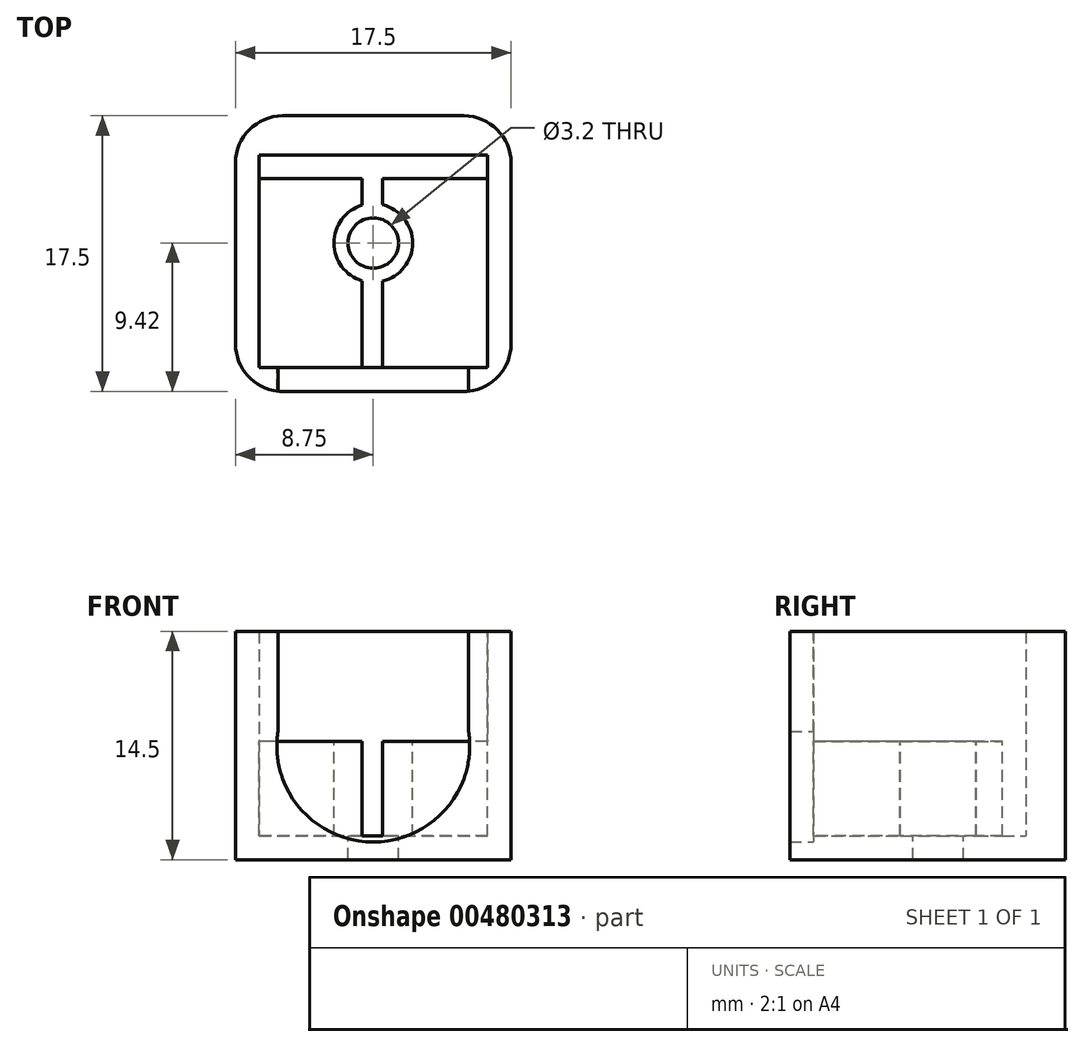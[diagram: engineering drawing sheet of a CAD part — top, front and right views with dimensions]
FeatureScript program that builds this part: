
annotation { "Feature Type Name" : "Feature", "Feature Type Description" : "" }
export const myFeature = defineFeature(function(context is Context, id is Id, definition is map)
    precondition{}
    {
        {
            var Q0;
            Q0=qCreatedBy(makeId("Front.planeOp"),FACE);
            var sketch = newSketch(context, id + "F0", { "sketchPlane" : qUnion([Q0])});
            skLineSegment(sketch, "E0.bottom", {"start": v(-7.25, 7.25) * mm, "end": v(7.25, 7.25) * mm});
            skLineSegment(sketch, "E0.top", {"start": v(-7.25, -7.25) * mm, "end": v(7.25, -7.25) * mm});
            skLineSegment(sketch, "E0.left", {"start": v(-7.25, 7.25) * mm, "end": v(-7.25, -7.25) * mm});
            skLineSegment(sketch, "E0.right", {"start": v(7.25, 7.25) * mm, "end": v(7.25, -7.25) * mm});
            skPoint(sketch, "E0.middle", {"position": v(0, 0) * mm});
            skEllipse(sketch, "E1", {"center": v(0, 0) * mm, "majorRadius": 6.12 * mm, "minorRadius": 6.13 * mm, "majorAxis": v(1, 0)});
            skLineSegment(sketch, "E2", {"start": v(-6.06, 0.91) * mm, "end": v(-6.06, 7.25) * mm});
            skLineSegment(sketch, "E3", {"start": v(6.06, 0.91) * mm, "end": v(6.06, 7.25) * mm});
            skSolve(sketch);
        }
        {
            var Q0;
            Q0=makeQuery(id+"F0.imprint","IMPRINT",FACE,{"disambiguationData":[TD([[makeQuery(id+"F0.imprint","IMPRINT",EDGE,{"derivedFrom":sQuery(id+"F0.wireOp",EDGE,"E0.bottom")}),-1.0]])]});
            extrude(context, id + "F1", {"entities" : qUnion([Q0]), "depth" : 1.5 * mm, "offsetDistance" : 25 * mm});
        }
        {
            var Q0;
            Q0=makeQuery(id+"F1.opExtrude","SWEPT_FACE",FACE,{"disambiguationData":[OSD([sQuery(id+"F0.wireOp",EDGE,"E0.right")])]});
            var sketch = newSketch(context, id + "F2", { "sketchPlane" : qUnion([Q0])});
            skLineSegment(sketch, "E4.0", {"start": v(-1.5, 7.25) * mm, "end": v(-1.5, -7.25) * mm});
            skLineSegment(sketch, "E5", {"start": v(-1.5, 7.25) * mm, "end": v(13.5, 7.25) * mm});
            skLineSegment(sketch, "E6", {"start": v(-1.5, -7.25) * mm, "end": v(13.5, -7.25) * mm});
            skPoint(sketch, "E6.endSnap0", {"position": v(-0.75, -7.25) * mm});
            skLineSegment(sketch, "E7", {"start": v(13.5, -7.25) * mm, "end": v(13.5, 7.25) * mm});
            skSolve(sketch);
        }
        {
            var Q0;
            {var subQ2=sQuery(id+"F2.wireOp",EDGE,"E7");Q0=makeQuery(id+"F2.imprint","IMPRINT",FACE,{"disambiguationData":[TD([[makeQuery(id+"F2.imprint","IMPRINT",EDGE,{"derivedFrom":subQ2}),1.0]])]});}
            var Q1;
            {var subQ0=sQuery(id+"F2.wireOp",EDGE,"E4.0");Q1=makeQuery(id+"F2.imprint","IMPRINT",FACE,{"disambiguationData":[TD([[makeQuery(id+"F2.imprint","IMPRINT",EDGE,{"derivedFrom":subQ0}),1.0]])]});}
            extrude(context, id + "F3", {"entities" : qUnion([Q0, Q1]), "operationType" : NewBodyOperationType.ADD, "depth" : 1.5 * mm, "offsetDistance" : 25 * mm});
        }
        {
            var Q0;
            Q0=makeQuery(id+"F1.opExtrude","SWEPT_FACE",FACE,{"disambiguationData":[OSD([sQuery(id+"F0.wireOp",EDGE,"E0.left")])]});
            var sketch = newSketch(context, id + "F4", { "sketchPlane" : qUnion([Q0])});
            skLineSegment(sketch, "E8.0", {"start": v(1.5, 7.25) * mm, "end": v(1.5, -7.25) * mm});
            skLineSegment(sketch, "E9", {"start": v(1.5, 7.25) * mm, "end": v(-13.5, 7.25) * mm});
            skLineSegment(sketch, "E10", {"start": v(-13.5, 7.25) * mm, "end": v(-13.5, -7.25) * mm});
            skLineSegment(sketch, "E11", {"start": v(-13.5, -7.25) * mm, "end": v(1.5, -7.25) * mm});
            skSolve(sketch);
        }
        {
            var Q0;
            {var subQ0=sQuery(id+"F4.wireOp",EDGE,"E8.0");Q0=makeQuery(id+"F4.imprint","IMPRINT",FACE,{"disambiguationData":[TD([[makeQuery(id+"F4.imprint","IMPRINT",EDGE,{"derivedFrom":subQ0}),-1.0]])]});}
            var Q1;
            {var subQ2=sQuery(id+"F4.wireOp",EDGE,"E10");Q1=makeQuery(id+"F4.imprint","IMPRINT",FACE,{"disambiguationData":[TD([[makeQuery(id+"F4.imprint","IMPRINT",EDGE,{"derivedFrom":subQ2}),1.0]])]});}
            extrude(context, id + "F5", {"entities" : qUnion([Q0, Q1]), "operationType" : NewBodyOperationType.ADD, "depth" : 1.5 * mm, "offsetDistance" : 25 * mm});
        }
        {
            var Q0;
            Q0=makeQuery(id+"F5.opExtrude","SWEPT_FACE",FACE,{"disambiguationData":[OSD([sQuery(id+"F4.wireOp",EDGE,"E10")])]});
            var sketch = newSketch(context, id + "F6", { "sketchPlane" : qUnion([Q0])});
            skLineSegment(sketch, "E12.0", {"start": v(-8.75, -7.25) * mm, "end": v(-8.75, 7.25) * mm});
            skLineSegment(sketch, "E13.0", {"start": v(8.75, 7.25) * mm, "end": v(8.75, -7.25) * mm});
            skLineSegment(sketch, "E14", {"start": v(-8.75, 7.25) * mm, "end": v(8.75, 7.25) * mm});
            skLineSegment(sketch, "E15", {"start": v(8.75, -7.25) * mm, "end": v(-8.75, -7.25) * mm});
            skSolve(sketch);
        }
        {
            var Q0;
            {var subQ0=sQuery(id+"F6.wireOp",EDGE,"E12.0");Q0=makeQuery(id+"F6.imprint","IMPRINT",FACE,{"disambiguationData":[TD([[makeQuery(id+"F6.imprint","IMPRINT",EDGE,{"derivedFrom":subQ0}),-1.0]])]});}
            var Q1;
            {var subQ0=sQuery(id+"F6.wireOp",EDGE,"E13.0");Q1=makeQuery(id+"F6.imprint","IMPRINT",FACE,{"disambiguationData":[TD([[makeQuery(id+"F6.imprint","IMPRINT",EDGE,{"derivedFrom":subQ0}),-1.0]])]});}
            extrude(context, id + "F7", {"entities" : qUnion([Q0, Q1]), "operationType" : NewBodyOperationType.ADD, "depth" : 2.5 * mm, "offsetDistance" : 25 * mm});
        }
        {
            var Q0;
            Q0=makeQuery(id+"F7.boolean.opBoolean","MERGE",FACE,{"derivedFrom":[makeQuery(id+"F5.boolean.opBoolean","MERGE",FACE,{"derivedFrom":[makeQuery(id+"F3.boolean.opBoolean","MERGE",FACE,{"derivedFrom":[makeQuery(id+"F1.opExtrude","SWEPT_FACE",FACE,{"disambiguationData":[OSD([sQuery(id+"F0.wireOp",EDGE,"E0.top")])]}),makeQuery(id+"F3.opExtrude","SWEPT_FACE",FACE,{"disambiguationData":[OSD([sQuery(id+"F2.wireOp",EDGE,"E6")])]})]}),makeQuery(id+"F5.opExtrude","SWEPT_FACE",FACE,{"disambiguationData":[OSD([sQuery(id+"F4.wireOp",EDGE,"E11")])]})]}),makeQuery(id+"F7.opExtrude","SWEPT_FACE",FACE,{"disambiguationData":[OSD([sQuery(id+"F6.wireOp",EDGE,"E15")])]})]});
            var sketch = newSketch(context, id + "F8", { "sketchPlane" : qUnion([Q0])});
            skPoint(sketch, "E16.0", {"position": v(0, -13.5) * mm});
            skLineSegment(sketch, "E17.0", {"start": v(-7.25, -13.5) * mm, "end": v(7.25, -13.5) * mm});
            skLineSegment(sketch, "E18.0", {"start": v(7.25, 0) * mm, "end": v(7.25, -13.5) * mm});
            skLineSegment(sketch, "E19.0", {"start": v(-7.25, 0) * mm, "end": v(7.25, 0) * mm});
            skLineSegment(sketch, "E20.0", {"start": v(-7.25, 0) * mm, "end": v(-7.25, -13.5) * mm});
            skSolve(sketch);
        }
        {
            var Q0;
            Q0=makeQuery(id+"F8.imprint","IMPRINT",FACE,{"disambiguationData":[TD([[makeQuery(id+"F8.imprint","IMPRINT",EDGE,{"derivedFrom":sQuery(id+"F8.wireOp",EDGE,"E17.0")}),1.0]])]});
            extrude(context, id + "F9", {"entities" : qUnion([Q0]), "operationType" : NewBodyOperationType.ADD, "oppositeDirection" : true, "depth" : 1.5 * mm, "offsetDistance" : 25 * mm});
        }
        {
            var Q0;
            Q0=makeQuery(id+"F5.opExtrude","CAP_FACE",FACE,{"disambiguationData":[OSD([sQuery(id+"F4.wireOp",EDGE,"E8.0"),sQuery(id+"F4.wireOp",EDGE,"E9"),sQuery(id+"F4.wireOp",EDGE,"E10"),sQuery(id+"F4.wireOp",EDGE,"E11")])],"isStart":true});
            var sketch = newSketch(context, id + "F10", { "sketchPlane" : qUnion([Q0])});
            skLineSegment(sketch, "E21.0", {"start": v(13.5, 7.25) * mm, "end": v(13.5, -5.75) * mm});
            skLineSegment(sketch, "E22.0", {"start": v(0, -5.75) * mm, "end": v(13.5, -5.75) * mm});
            skLineSegment(sketch, "E23.0", {"start": v(0, 7.25) * mm, "end": v(13.5, 7.25) * mm});
            skLineSegment(sketch, "E24.0", {"start": v(0, 6.25) * mm, "end": v(0, -5.75) * mm});
            skLineSegment(sketch, "E25", {"start": v(12, -5.75) * mm, "end": v(12, 0.25) * mm});
            skLineSegment(sketch, "E26", {"start": v(12, 0.25) * mm, "end": v(0, 0.25) * mm});
            skLineSegment(sketch, "E27", {"start": v(0, 0.25) * mm, "end": v(0, -5.75) * mm});
            skSolve(sketch);
        }
        {
            var Q0;
            {var subQ0=sQuery(id+"F10.wireOp",EDGE,"E25");Q0=makeQuery(id+"F10.imprint","IMPRINT",FACE,{"disambiguationData":[TD([[makeQuery(id+"F10.imprint","IMPRINT",EDGE,{"derivedFrom":subQ0}),1.0]])]});}
            var Q1;
            Q1=makeQuery(id+"F3.opExtrude","CAP_FACE",FACE,{"disambiguationData":[OSD([sQuery(id+"F2.wireOp",EDGE,"E4.0"),sQuery(id+"F2.wireOp",EDGE,"E5"),sQuery(id+"F2.wireOp",EDGE,"E6"),sQuery(id+"F2.wireOp",EDGE,"E7")])],"isStart":true});
            extrude(context, id + "F11", {"entities" : qUnion([Q0]), "operationType" : NewBodyOperationType.ADD, "endBound" : BoundingType.UP_TO_SURFACE, "endBoundEntityFace" : qUnion([Q1]), "depth" : 25 * mm, "offsetDistance" : 25 * mm});
        }
        {
            var Q0;
            Q0=makeQuery(id+"F11.opExtrude","SWEPT_FACE",FACE,{"disambiguationData":[OSD([sQuery(id+"F10.wireOp",EDGE,"E26")])]});
            var sketch = newSketch(context, id + "F12", { "sketchPlane" : qUnion([Q0])});
            skLineSegment(sketch, "E28.0", {"start": v(7.25, 12) * mm, "end": v(-7.25, 12) * mm});
            skLineSegment(sketch, "E29.0", {"start": v(51.12, 0) * mm, "end": v(-51.12, 0) * mm});
            skLineSegment(sketch, "E30", {"start": v(-0.7, 12) * mm, "end": v(-0.7, 0) * mm});
            skLineSegment(sketch, "E31", {"start": v(-0.7, 0) * mm, "end": v(0.6, 0) * mm});
            skLineSegment(sketch, "E32", {"start": v(0.6, 0) * mm, "end": v(0.6, 12) * mm});
            skLineSegment(sketch, "E33", {"start": v(0.6, 12) * mm, "end": v(-0.7, 12) * mm});
            skSolve(sketch);
        }
        {
            var Q0;
            Q0=makeQuery(id+"F12.imprint","IMPRINT",FACE,{"disambiguationData":[TD([[makeQuery(id+"F12.imprint","IMPRINT",EDGE,{"derivedFrom":sQuery(id+"F12.wireOp",EDGE,"E30")}),1.0]])]});
            var Q1;
            Q1=makeQuery(id+"F11.boolean.opBoolean","SPLIT",FACE,{"disambiguationData":[TD([makeQuery(id+"F11.opExtrude","SWEPT_FACE",FACE,{"disambiguationData":[OSD([sQuery(id+"F10.wireOp",EDGE,"E25")])]})])],"derivedFrom":makeQuery(id+"F9.opExtrude","CAP_FACE",FACE,{"disambiguationData":[OSD([sQuery(id+"F8.wireOp",EDGE,"E17.0"),sQuery(id+"F8.wireOp",EDGE,"E18.0"),sQuery(id+"F8.wireOp",EDGE,"E19.0"),sQuery(id+"F8.wireOp",EDGE,"E20.0")])],"isStart":false})});
            extrude(context, id + "F13", {"entities" : qUnion([Q0]), "operationType" : NewBodyOperationType.REMOVE, "endBound" : BoundingType.UP_TO_SURFACE, "oppositeDirection" : true, "endBoundEntityFace" : qUnion([Q1]), "depth" : 25.4 * mm});
        }
        {
            var Q0;
            {var subQ0=sQuery(id+"F0.wireOp",EDGE,"E0.bottom");Q0=makeQuery(id+"F7.boolean.opBoolean","MERGE",FACE,{"derivedFrom":[makeQuery(id+"F3.boolean.opBoolean","MERGE",FACE,{"derivedFrom":[makeQuery(id+"F1.opExtrude","SWEPT_FACE",FACE,{"disambiguationData":[OSD([subQ0]),TDD([makeQuery(id+"F0.imprint","IMPRINT",EDGE,{"disambiguationData":[TD([[makeQuery(id+"F0.imprint","INTERSECT",VERTEX,{"derivedFrom":[subQ0,sQuery(id+"F0.wireOp",EDGE,"E0.right")]}),1.0]])],"derivedFrom":subQ0})])]}),makeQuery(id+"F3.opExtrude","SWEPT_FACE",FACE,{"disambiguationData":[OSD([sQuery(id+"F2.wireOp",EDGE,"E5")])]})]}),makeQuery(id+"F5.boolean.opBoolean","MERGE",FACE,{"derivedFrom":[makeQuery(id+"F1.opExtrude","SWEPT_FACE",FACE,{"disambiguationData":[OSD([subQ0]),TDD([makeQuery(id+"F0.imprint","IMPRINT",EDGE,{"disambiguationData":[TD([[makeQuery(id+"F0.imprint","INTERSECT",VERTEX,{"derivedFrom":[subQ0,sQuery(id+"F0.wireOp",EDGE,"E0.left")]}),-1.0]])],"derivedFrom":subQ0})])]}),makeQuery(id+"F5.opExtrude","SWEPT_FACE",FACE,{"disambiguationData":[OSD([sQuery(id+"F4.wireOp",EDGE,"E9")])]})]}),makeQuery(id+"F7.opExtrude","SWEPT_FACE",FACE,{"disambiguationData":[OSD([sQuery(id+"F6.wireOp",EDGE,"E14")])]})]});}
            var sketch = newSketch(context, id + "F14", { "sketchPlane" : qUnion([Q0])});
            skCircle(sketch, "E34", {"center": v(0, 7.92) * mm, "radius": 2.5 * mm});
            skCircle(sketch, "E35", {"center": v(0, 7.92) * mm, "radius": 1.6 * mm});
            skSolve(sketch);
        }
        {
            var Q0;
            Q0=makeQuery(id+"F14.imprint","IMPRINT",FACE,{"disambiguationData":[TD([[makeQuery(id+"F14.imprint","IMPRINT",EDGE,{"derivedFrom":sQuery(id+"F14.wireOp",EDGE,"E34")}),1.0]])]});
            var Q1;
            {var subQ2=makeQuery(id+"F9.opExtrude","CAP_FACE",FACE,{"disambiguationData":[OSD([sQuery(id+"F8.wireOp",EDGE,"E17.0"),sQuery(id+"F8.wireOp",EDGE,"E18.0"),sQuery(id+"F8.wireOp",EDGE,"E19.0"),sQuery(id+"F8.wireOp",EDGE,"E20.0")])],"isStart":false});Q1=makeQuery(id+"F13.boolean.opBoolean","MERGE",FACE,{"derivedFrom":[makeQuery(id+"F11.boolean.opBoolean","SPLIT",FACE,{"disambiguationData":[TD([makeQuery(id+"F11.opExtrude","SWEPT_FACE",FACE,{"disambiguationData":[OSD([sQuery(id+"F10.wireOp",EDGE,"E25")])]})])],"derivedFrom":subQ2}),makeQuery(id+"F11.boolean.opBoolean","SPLIT",FACE,{"disambiguationData":[TD([makeQuery(id+"F11.opExtrude","SWEPT_FACE",FACE,{"disambiguationData":[OSD([sQuery(id+"F10.wireOp",EDGE,"E27")])]})])],"derivedFrom":subQ2}),makeQuery(id+"F13.opExtrude","CAP_FACE",FACE,{"disambiguationData":[OSD([sQuery(id+"F12.wireOp",EDGE,"E30"),sQuery(id+"F12.wireOp",EDGE,"E31"),sQuery(id+"F12.wireOp",EDGE,"E32"),sQuery(id+"F12.wireOp",EDGE,"E33")])],"isStart":false})]});}
            extrude(context, id + "F15", {"entities" : qUnion([Q0]), "operationType" : NewBodyOperationType.REMOVE, "endBound" : BoundingType.UP_TO_SURFACE, "oppositeDirection" : true, "endBoundEntityFace" : qUnion([Q1]), "depth" : 25 * mm, "offsetDistance" : 25 * mm});
        }
        {
            var Q0;
            Q0=makeQuery(id+"F14.imprint","IMPRINT",FACE,{"disambiguationData":[TD([[makeQuery(id+"F14.imprint","IMPRINT",EDGE,{"derivedFrom":sQuery(id+"F14.wireOp",EDGE,"E35")}),1.0]])]});
            extrude(context, id + "F16", {"entities" : qUnion([Q0]), "operationType" : NewBodyOperationType.REMOVE, "endBound" : BoundingType.THROUGH_ALL, "oppositeDirection" : true, "depth" : 25 * mm, "offsetDistance" : 25 * mm});
        }
        {
            var Q0;
            Q0=makeQuery(id+"F3.opExtrude","CAP_EDGE",EDGE,{"disambiguationData":[OSD([sQuery(id+"F2.wireOp",EDGE,"E4.0")])],"isStart":false});
            var Q1;
            Q1=makeQuery(id+"F5.opExtrude","CAP_EDGE",EDGE,{"disambiguationData":[OSD([sQuery(id+"F4.wireOp",EDGE,"E8.0")])],"isStart":false});
            var Q2;
            Q2=makeQuery(id+"F7.opExtrude","CAP_EDGE",EDGE,{"disambiguationData":[OSD([sQuery(id+"F6.wireOp",EDGE,"E13.0")])],"isStart":false});
            var Q3;
            Q3=makeQuery(id+"F7.opExtrude","CAP_EDGE",EDGE,{"disambiguationData":[OSD([sQuery(id+"F6.wireOp",EDGE,"E12.0")])],"isStart":false});
            fillet(context, id + "F17", {"entities" : qUnion([Q0, Q1, Q2, Q3]), "radius" : 3 * mm, "tangentPropagation" : true, "allowEdgeOverflow" : false});
        }
    });
